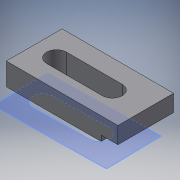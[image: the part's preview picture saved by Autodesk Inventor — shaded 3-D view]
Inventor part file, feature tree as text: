
AUTODESK INVENTOR PART (.ipt)
format: ipt  version: 2019 (Build 230136000, 136)  size: 126,464 bytes
history: native  units: mm
features: extrude x2, sketch x2, fillet x1
ambient origin geometry x8: Origin, YZ Plane, XZ Plane, XY Plane, X Axis, Y Axis, Z Axis, Center Point
bodies: Solid1 (feature_tree)
feature tree (5):
  extrude  "Extrusion1"  Depth=8.0mm
  extrude  "Extrusion3"  Depth=1.778mm
  fillet  "Fillet2"  Radius=2.0mm
  sketch  "Sketch1"  dims[d3=2.0mm d4=0.0mm d19=8.0mm]
  sketch  "Sketch4"  dims[d20=5.0mm d21=1.778mm d22=2.0mm d23=3.0mm d24=0.5mm d25=1.5mm d26=10.0mm d27=0.0mm d28=0.5mm]
